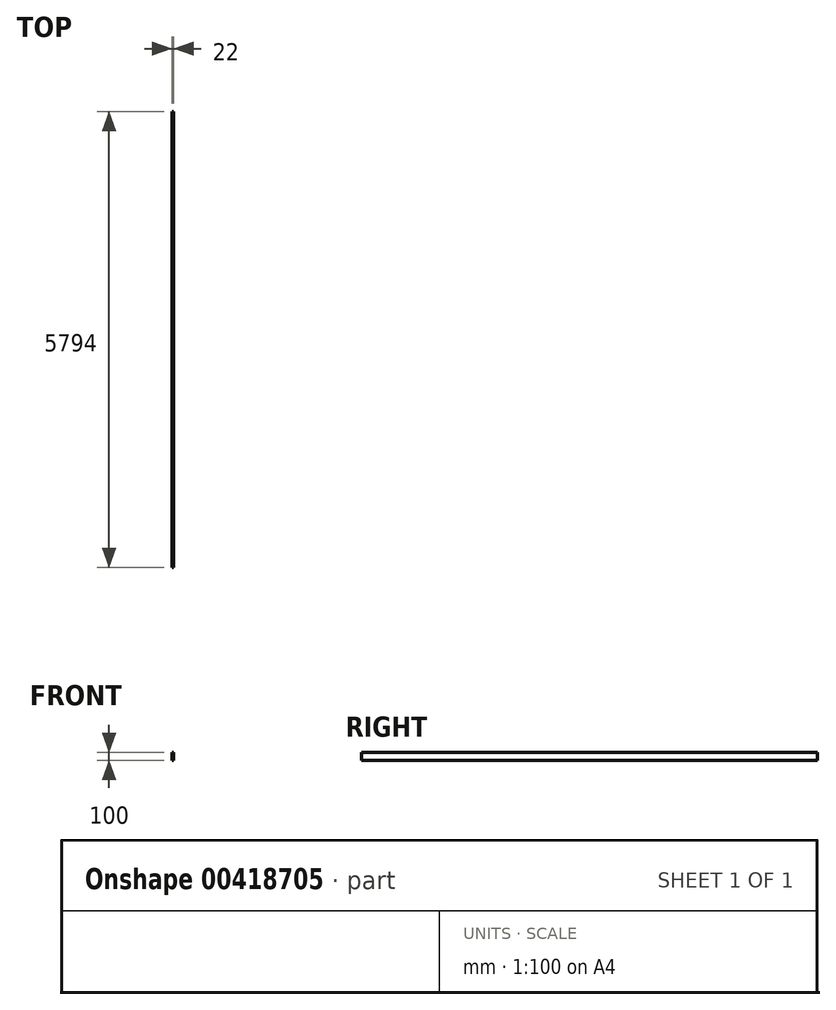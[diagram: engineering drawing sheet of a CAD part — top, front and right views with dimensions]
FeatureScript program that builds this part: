
annotation { "Feature Type Name" : "Feature", "Feature Type Description" : "" }
export const myFeature = defineFeature(function(context is Context, id is Id, definition is map)
    precondition{}
    {
        {
            var Q0;
            Q0=qCreatedBy(makeId("Front.planeOp"),FACE);
            var sketch = newSketch(context, id + "F0", { "sketchPlane" : qUnion([Q0])});
            skLineSegment(sketch, "E0.bottom", {"start": v(11, 50) * mm, "end": v(-11, 50) * mm});
            skLineSegment(sketch, "E0.top", {"start": v(11, -50) * mm, "end": v(-11, -50) * mm});
            skLineSegment(sketch, "E0.left", {"start": v(11, 50) * mm, "end": v(11, -50) * mm});
            skLineSegment(sketch, "E0.right", {"start": v(-11, 50) * mm, "end": v(-11, -50) * mm});
            skPoint(sketch, "E0.middle", {"position": v(0, 0) * mm});
            skSolve(sketch);
        }
        {
            var Q0;
            Q0=qSketchRegion(id+"F0",true);
            extrude(context, id + "F1", {"entities" : qUnion([Q0]), "endBound" : BoundingType.SYMMETRIC, "depth" : (5750 + 44) * mm});
        }
    });
